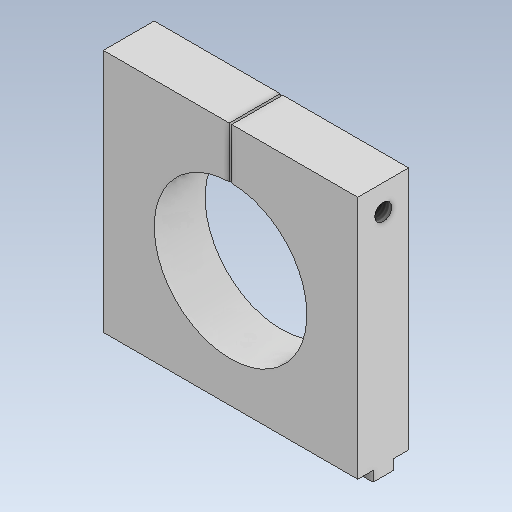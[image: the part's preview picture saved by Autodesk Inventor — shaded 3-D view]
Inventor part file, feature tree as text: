
AUTODESK INVENTOR PART (.ipt)
format: ipt  version: 2021 (Build 250183000, 183)  size: 159,744 bytes
history: native  units: mm
features: sketch x6, extrude x3, hole x3, projected_geometry x2
ambient origin geometry x8: Origin, YZ Plane, XZ Plane, XY Plane, X Axis, Y Axis, Z Axis, Center Point
bodies: Solid1 (feature_tree)
feature tree (14):
  extrude  "Extrusion1"  Depth=100.0mm
  extrude  "Extrusion2"  Depth=20.0mm TaperAngle=0.0deg
  extrude  "Extrusion3"  Depth=4.0mm
  hole  "Hole1"  [1 undecoded]
  hole  "Hole2"  [1 undecoded]
  hole  "Hole3"  [1 undecoded]
  sketch  "Sketch1"  dims[d0=100.0mm d1=100.0mm]
  sketch  "Sketch2"  dims[d2=60.0mm d3=20.0mm d4=0.0mm]
  projected_geometry  "Projected Loop1"
  sketch  "Sketch3"  dims[d5=4.0mm d6=4.0mm]
  projected_geometry  "Projected Loop2"
  sketch  "Sketch4"  dims[d7=4.0mm d8=0.0mm d9=0.5mm]
  sketch  "Sketch5"  dims[d10=0.5mm d11=4.0mm d12=0.0mm]
  sketch  "Sketch6"  dims[d13=10.0mm d14=10.0mm d15=6.647mm d16=50.0mm d17=4.0mm d18=2.0mm d19=90.0deg d20=110.0mm d21=20.594885mm d22=10.0mm d23=10.0mm d24=6.647mm d25=20.0mm d26=4.0mm d27=2.0mm d28=90.0deg d29=30.0mm d30=20.594885mm d31=10.0mm d32=10.0mm d33=6.647mm d34=20.0mm d35=4.0mm d36=2.0mm d37=90.0deg d38=30.0mm d39=20.594885mm]
note: 3 required parameter values undecoded (feature->parameter linkage not recoverable at this tier; creation-order binding heuristic only, values carry confidence <= 0.55)
